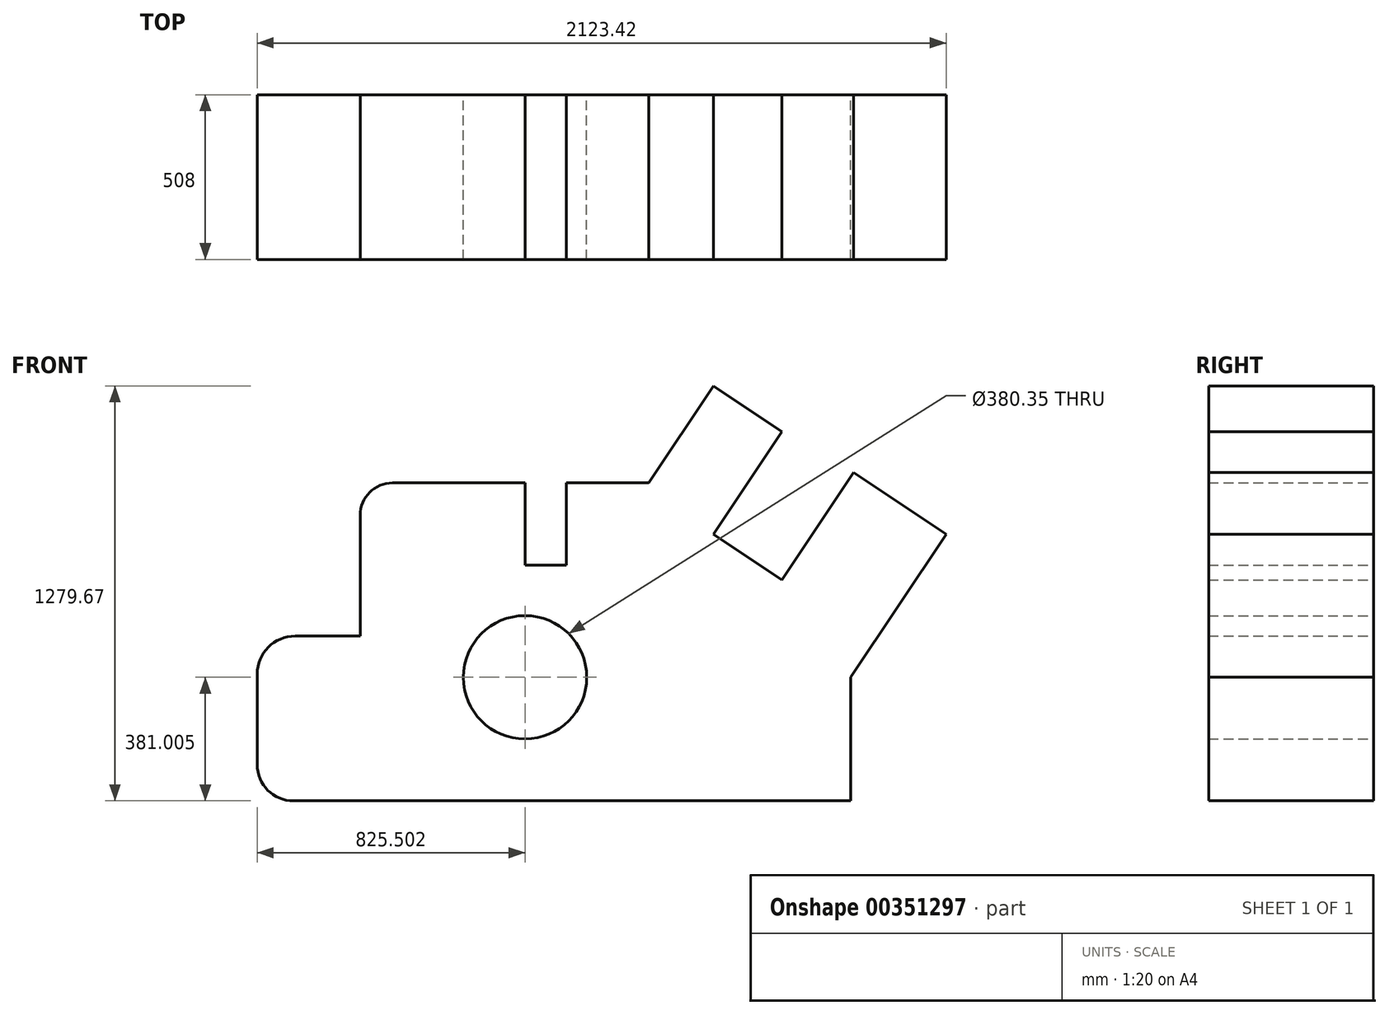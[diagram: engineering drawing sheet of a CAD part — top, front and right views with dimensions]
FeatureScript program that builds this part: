
annotation { "Feature Type Name" : "Feature", "Feature Type Description" : "" }
export const myFeature = defineFeature(function(context is Context, id is Id, definition is map)
    precondition{}
    {
        {
            var Q0;
            Q0=qCreatedBy(makeId("Front.planeOp"),FACE);
            var sketch = newSketch(context, id + "F0", { "sketchPlane" : qUnion([Q0])});
            skLineSegment(sketch, "E0", {"start": v(-762.32, -630.78) * mm, "end": v(-962.66, -630.78) * mm});
            skLineSegment(sketch, "E1", {"start": v(-1079.82, -747.93) * mm, "end": v(-1079.82, -1027.16) * mm});
            skLineSegment(sketch, "E2", {"start": v(-968.2, -1138.78) * mm, "end": v(749.76, -1138.78) * mm});
            skLineSegment(sketch, "E3", {"start": v(749.76, -1138.78) * mm, "end": v(749.76, -757.78) * mm});
            skLineSegment(sketch, "E4", {"start": v(749.76, -757.78) * mm, "end": v(1043.6, -317.01) * mm});
            skLineSegment(sketch, "E5", {"start": v(1043.6, -317.01) * mm, "end": v(758.1, -126.68) * mm});
            skLineSegment(sketch, "E6", {"start": v(758.1, -126.68) * mm, "end": v(537.3, -457.9) * mm});
            skLineSegment(sketch, "E7", {"start": v(537.3, -457.9) * mm, "end": v(325.95, -317.01) * mm});
            skLineSegment(sketch, "E8", {"start": v(325.95, -317.01) * mm, "end": v(537.3, 0) * mm});
            skLineSegment(sketch, "E9", {"start": v(537.3, 0) * mm, "end": v(325.95, 140.9) * mm});
            skLineSegment(sketch, "E10", {"start": v(325.95, 140.9) * mm, "end": v(126.68, -158.01) * mm});
            skLineSegment(sketch, "E11", {"start": v(126.68, -158.01) * mm, "end": v(-127.32, -158.01) * mm});
            skLineSegment(sketch, "E12", {"start": v(-127.32, -158.01) * mm, "end": v(-127.32, -412.01) * mm});
            skLineSegment(sketch, "E13", {"start": v(-127.32, -412.01) * mm, "end": v(-254.32, -412.01) * mm});
            skLineSegment(sketch, "E14", {"start": v(-254.32, -412.01) * mm, "end": v(-254.32, -158.01) * mm});
            skLineSegment(sketch, "E15", {"start": v(-254.32, -158.01) * mm, "end": v(-662.49, -158.01) * mm});
            skLineSegment(sketch, "E16", {"start": v(-762.32, -630.78) * mm, "end": v(-762.32, -257.84) * mm});
            skCircle(sketch, "E17", {"center": v(-254.32, -757.78) * mm, "radius": 190.18 * mm});
            skArc(sketch, "E18", {"start": v(-962.66, -630.78) * mm, "mid": v(-1045.5, -665.09) * mm, "end": v(-1079.82, -747.93) * mm});
            skArc(sketch, "E19", {"start": v(-1079.82, -1027.16) * mm, "mid": v(-1047.13, -1106.08) * mm, "end": v(-968.2, -1138.78) * mm});
            skArc(sketch, "E20", {"start": v(-662.49, -158.01) * mm, "mid": v(-733.08, -187.25) * mm, "end": v(-762.32, -257.84) * mm});
            skSolve(sketch);
        }
        {
            var Q0;
            Q0 = qSketchRegion(id + "F0", true);
            extrude(context, id + "F1", {"entities" : qUnion([Q0]), "depth" : 508 * mm});
        }
    });
